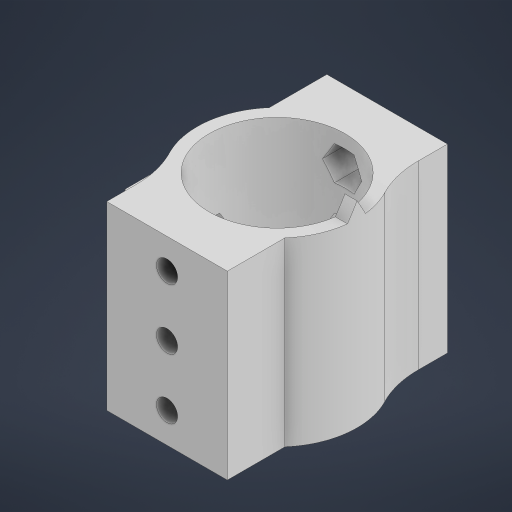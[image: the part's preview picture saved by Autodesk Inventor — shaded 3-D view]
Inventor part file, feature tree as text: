
AUTODESK INVENTOR PART (.ipt)
format: ipt  version: 2023 (Build 270158000, 158)  size: 333,824 bytes
history: native  units: mm
features: extrude x8, sketch x7, plane x3, fillet x2, projected_geometry x1
ambient origin geometry x8: Origin, YZ Plane, XZ Plane, XY Plane, X Axis, Y Axis, Z Axis, Center Point
bodies: Solid1 (feature_tree)
feature tree (21):
  extrude  "Extrusion1"  Depth=2.0mm
  plane  "Work Plane1"
  sketch  "Sketch2"  dims[d2=30.0mm d3=0.0mm d4=15.5mm]
  extrude  "Extrusion3"  Depth=30.0mm
  plane  "Work Plane2"
  extrude  "Extrusion4"  TaperAngle=60.0deg  [1 undecoded]
  sketch  "Sketch7"  dims[d12=12.25mm d13=0.0mm d14=-20.25mm d16=0.2mm]
  extrude  "Extrusion5"  TaperAngle=60.0deg  [1 undecoded]
  extrude  "Extrusion6"  [1 undecoded]
  fillet  "Fillet1"  Radius=0.2mm
  sketch  "Sketch8"  dims[d18=10.25mm d19=0.0mm d20=6.5mm d21=60.0mm d23=360.0deg]
  extrude  "Extrusion8"  Depth=6.5mm
  fillet  "Fillet2"  Radius=60.0mm
  plane  "Work Plane3"
  extrude  "Extrusion9"  Depth=10.0mm TaperAngle=0.0deg
  extrude  "Extrusion10"  Depth=5.0mm TaperAngle=0.0deg
  sketch  "Sketch1"  dims[d0=22.5mm d1=2.0mm]
  projected_geometry  "Projected Loop1"
  sketch  "Sketch3"  dims[d5=60.0deg d7=60.0deg]
  sketch  "Sketch5"  dims[d8=3.0mm d11=60.0deg]
  sketch  "Sketch10"  dims[d25=3.6mm d26=10.0mm d27=0.0mm d28=5.0mm d29=0.0mm d30=3.0mm d33=20.0mm d34=5.0mm d37=9.75mm d38=0.0mm d39=16.0mm d40=3.5mm d41=10.0mm d42=54.5mm d43=0.0mm d44=6.5mm d45=60.0mm d47=360.0deg d49=60.0mm d51=360.0deg d53=60.0mm d55=360.0deg d57=31.5mm d58=0.0mm d59=10.0mm d31=0.5mm d32=0.872665mm]
note: 3 required parameter values undecoded (feature->parameter linkage not recoverable at this tier; creation-order binding heuristic only, values carry confidence <= 0.55)
